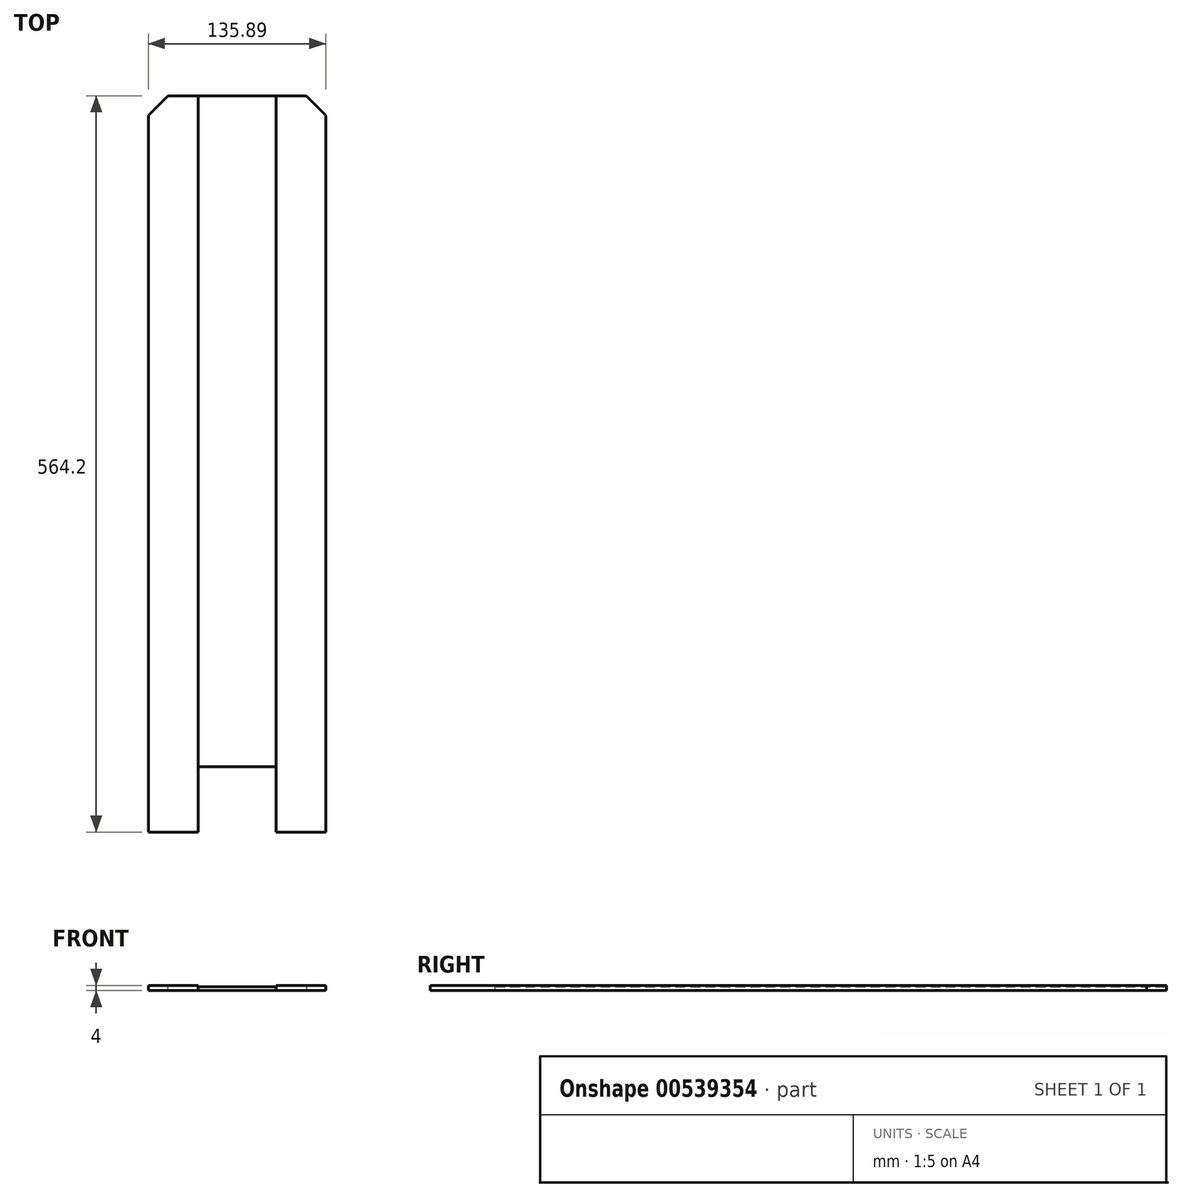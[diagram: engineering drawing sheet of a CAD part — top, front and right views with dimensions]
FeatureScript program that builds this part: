
annotation { "Feature Type Name" : "Feature", "Feature Type Description" : "" }
export const myFeature = defineFeature(function(context is Context, id is Id, definition is map)
    precondition{}
    {
        {
            var Q0;
            Q0=qCreatedBy(makeId("Front.planeOp"),FACE);
            var sketch = newSketch(context, id + "F0", { "sketchPlane" : qUnion([Q0])});
            skLineSegment(sketch, "E0", {"start": v(0, 0) * mm, "end": v(59.7, 0) * mm});
            skLineSegment(sketch, "E1", {"start": v(0, 0) * mm, "end": v(0, 3) * mm});
            skLineSegment(sketch, "E2", {"start": v(0, 3) * mm, "end": v(59.7, 3) * mm});
            skLineSegment(sketch, "E3", {"start": v(59.7, 3) * mm, "end": v(59.7, 0) * mm});
            skSolve(sketch);
        }
        {
            var Q0;
            Q0=makeQuery(id+"F0.imprint","IMPRINT",FACE,{"disambiguationData":[TD([[makeQuery(id+"F0.imprint","IMPRINT",EDGE,{"derivedFrom":sQuery(id+"F0.wireOp",EDGE,"E0")}),1.0]])]});
            extrude(context, id + "F1", {"entities" : qUnion([Q0]), "depth" : 514.2 * mm, "offsetDistance" : 25.4 * mm});
        }
        {
            var Q0;
            Q0=makeQuery(id+"F1.opExtrude","CAP_FACE",FACE,{"disambiguationData":[OSD([sQuery(id+"F0.wireOp",EDGE,"E0"),sQuery(id+"F0.wireOp",EDGE,"E1"),sQuery(id+"F0.wireOp",EDGE,"E2"),sQuery(id+"F0.wireOp",EDGE,"E3")])],"isStart":true});
            var sketch = newSketch(context, id + "F2", { "sketchPlane" : qUnion([Q0])});
            skLineSegment(sketch, "E4", {"start": v(-59.7, 0) * mm, "end": v(-97.8, 0) * mm});
            skLineSegment(sketch, "E5", {"start": v(0, 3) * mm, "end": v(0, 0) * mm});
            skLineSegment(sketch, "E6", {"start": v(-59.7, 3) * mm, "end": v(-59.7, 0) * mm});
            skLineSegment(sketch, "E7", {"start": v(-97.8, 0) * mm, "end": v(-97.8, 4) * mm});
            skLineSegment(sketch, "E8", {"start": v(-97.8, 1.2) * mm, "end": v(-97.8, 4) * mm});
            skLineSegment(sketch, "E9", {"start": v(-97.8, 4) * mm, "end": v(-59.7, 4) * mm});
            skLineSegment(sketch, "E10", {"start": v(-59.7, 4) * mm, "end": v(-59.7, 3) * mm});
            skLineSegment(sketch, "E11", {"start": v(-59.7, 0) * mm, "end": v(-59.7, 4) * mm});
            skLineSegment(sketch, "E12", {"start": v(0, 0) * mm, "end": v(38.1, 0) * mm});
            skPoint(sketch, "E13.orphan", {"position": v(38.1, -0.6) * mm});
            skLineSegment(sketch, "E14", {"start": v(38.1, 0) * mm, "end": v(38.1, 4) * mm});
            skLineSegment(sketch, "E15", {"start": v(38.1, 4) * mm, "end": v(0, 4) * mm});
            skLineSegment(sketch, "E16", {"start": v(0, 4) * mm, "end": v(0, 0) * mm});
            skSolve(sketch);
        }
        {
            var Q0;
            Q0 = qSketchRegion(id + "F2", true);
            extrude(context, id + "F3", {"entities" : qUnion([Q0]), "operationType" : NewBodyOperationType.ADD, "oppositeDirection" : true, "depth" : 564.2 * mm, "offsetDistance" : 25 * mm});
        }
        {
            var Q0;
            Q0=makeQuery(id+"F3.opExtrude","CAP_EDGE",EDGE,{"disambiguationData":[OSD([sQuery(id+"F2.wireOp",EDGE,"E7"),sQuery(id+"F2.wireOp",EDGE,"E8")])],"isStart":true});
            var Q1;
            Q1=makeQuery(id+"F3.opExtrude","CAP_EDGE",EDGE,{"disambiguationData":[OSD([sQuery(id+"F2.wireOp",EDGE,"E14")])],"isStart":true});
            chamfer(context, id + "F4", {"entities" : qUnion([Q0, Q1]), "width" : 15 * mm, "tangentPropagation" : true});
        }
    });
